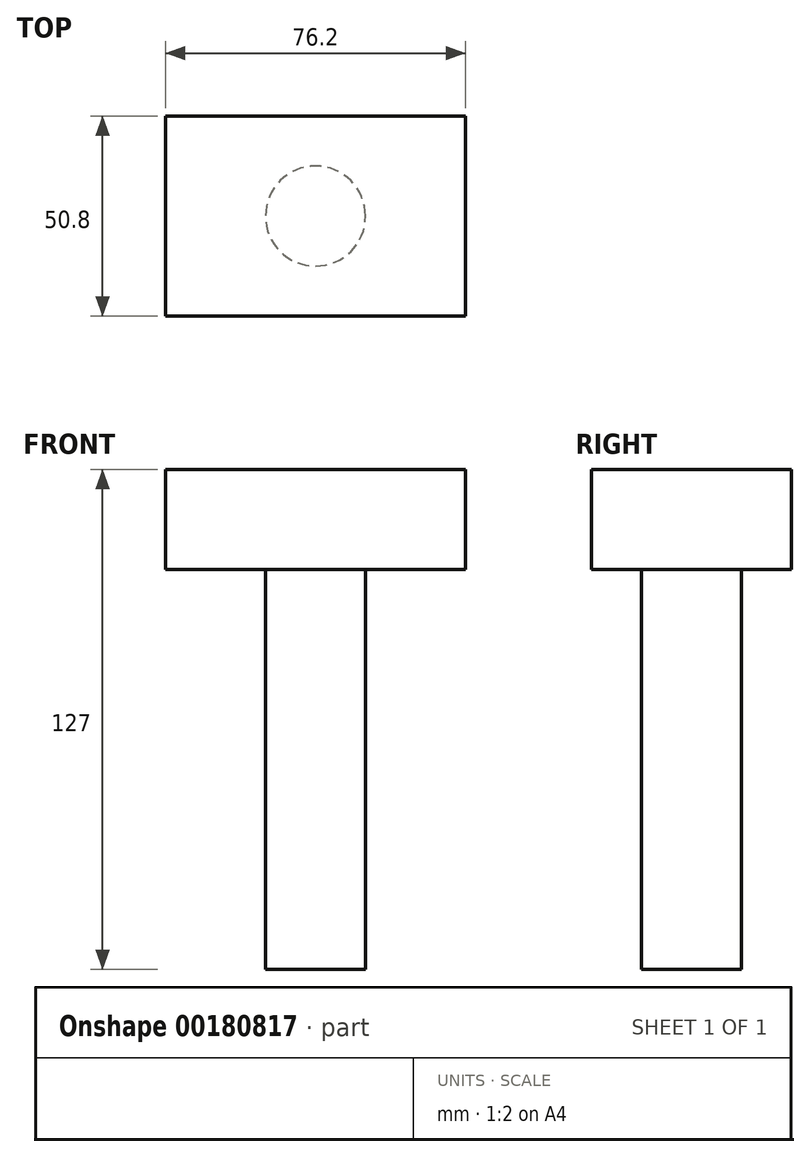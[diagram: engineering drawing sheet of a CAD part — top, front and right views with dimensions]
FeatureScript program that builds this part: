
annotation { "Feature Type Name" : "Feature", "Feature Type Description" : "" }
export const myFeature = defineFeature(function(context is Context, id is Id, definition is map)
    precondition{}
    {
        {
            var Q0;
            Q0=qCreatedBy(makeId("Top.planeOp"),FACE);
            var sketch = newSketch(context, id + "F0", { "sketchPlane" : qUnion([Q0])});
            skLineSegment(sketch, "E0.bottom", {"start": v(-38.1, 25.4) * mm, "end": v(38.1, 25.4) * mm});
            skLineSegment(sketch, "E0.top", {"start": v(-38.1, -25.4) * mm, "end": v(38.1, -25.4) * mm});
            skLineSegment(sketch, "E0.left", {"start": v(-38.1, 25.4) * mm, "end": v(-38.1, -25.4) * mm});
            skLineSegment(sketch, "E0.right", {"start": v(38.1, 25.4) * mm, "end": v(38.1, -25.4) * mm});
            skPoint(sketch, "E0.middle", {"position": v(0, 0) * mm});
            skSolve(sketch);
        }
        {
            var Q0;
            Q0 = qSketchRegion(id + "F0", true);
            extrude(context, id + "F1", {"entities" : qUnion([Q0]), "depth" : 25.4 * mm});
        }
        {
            var Q0;
            Q0=makeQuery(id+"F1.opExtrude","CAP_FACE",FACE,{"disambiguationData":[OSD([sQuery(id+"F0.wireOp",EDGE,"E0.bottom"),sQuery(id+"F0.wireOp",EDGE,"E0.top"),sQuery(id+"F0.wireOp",EDGE,"E0.left"),sQuery(id+"F0.wireOp",EDGE,"E0.right")])],"isStart":true});
            var sketch = newSketch(context, id + "F2", { "sketchPlane" : qUnion([Q0])});
            skCircle(sketch, "E1", {"center": v(0, 0) * mm, "radius": 12.7 * mm});
            skSolve(sketch);
        }
        {
            var Q0;
            Q0=makeQuery(id+"F2.imprint","IMPRINT",FACE,{"disambiguationData":[TD([[makeQuery(id+"F2.imprint","IMPRINT",EDGE,{"derivedFrom":sQuery(id+"F2.wireOp",EDGE,"E1")}),1.0]])]});
            extrude(context, id + "F3", {"entities" : qUnion([Q0]), "operationType" : NewBodyOperationType.ADD, "depth" : 101.6 * mm});
        }
    });
